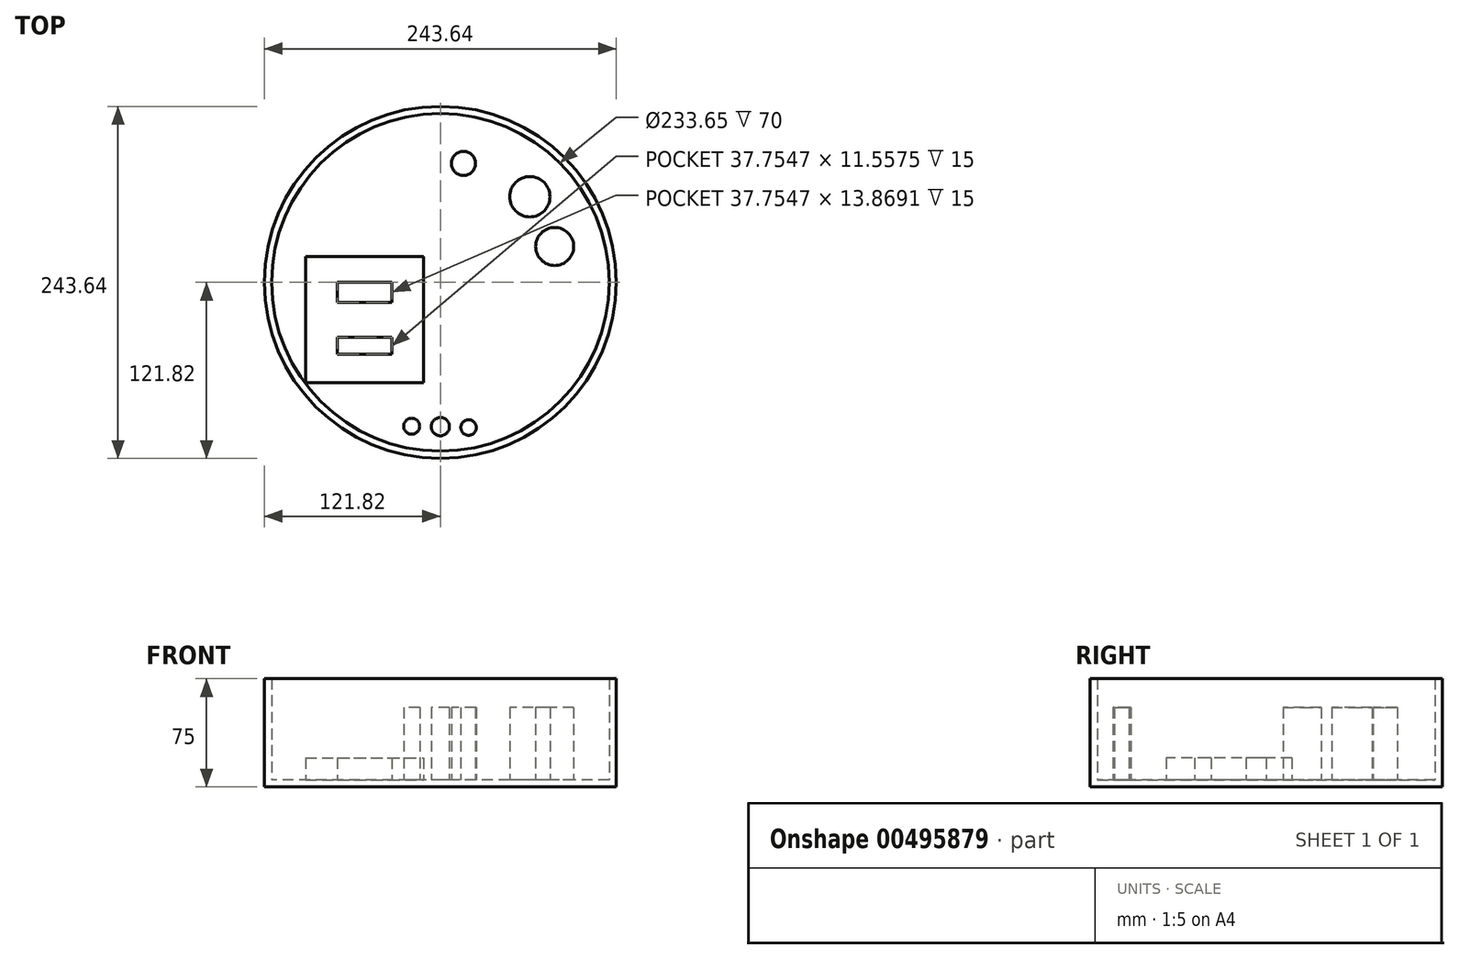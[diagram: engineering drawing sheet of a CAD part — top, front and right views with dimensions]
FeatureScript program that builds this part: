
annotation { "Feature Type Name" : "Feature", "Feature Type Description" : "" }
export const myFeature = defineFeature(function(context is Context, id is Id, definition is map)
    precondition{}
    {
        {
            var Q0;
            Q0=qCreatedBy(makeId("Top.planeOp"),FACE);
            var sketch = newSketch(context, id + "F0", { "sketchPlane" : qUnion([Q0])});
            skCircle(sketch, "E0", {"center": v(0, 0) * mm, "radius": 121.82 * mm});
            skSolve(sketch);
        }
        {
            var Q0;
            Q0=makeQuery(id+"F0.imprint","IMPRINT",FACE,{"disambiguationData":[TD([[makeQuery(id+"F0.imprint","IMPRINT",EDGE,{"derivedFrom":sQuery(id+"F0.wireOp",EDGE,"E0")}),1.0]])]});
            extrude(context, id + "F1", {"entities" : qUnion([Q0]), "depth" : 75 * mm});
        }
        {
            var Q0;
            Q0=makeQuery(id+"F1.opExtrude","CAP_FACE",FACE,{"disambiguationData":[OSD([sQuery(id+"F0.wireOp",EDGE,"E0")])],"isStart":false});
            shell(context, id + "F2", {"entities" : qUnion([Q0]), "thickness" : 5 * mm});
        }
        {
            var Q0;
            {var subQ0=sQuery(id+"F0.wireOp",EDGE,"E0");Q0=makeQuery(id+"F2.opShell","OFFSET_FACE",FACE,{"disambiguationData":[OSD([subQ0]),TDD([makeQuery(id+"F1.opExtrude","CAP_FACE",FACE,{"disambiguationData":[OSD([subQ0])],"isStart":true})])]});}
            var sketch = newSketch(context, id + "F3", { "sketchPlane" : qUnion([Q0])});
            skCircle(sketch, "E1", {"center": v(16.06, 82.36) * mm, "radius": 8.35 * mm});
            skCircle(sketch, "E2", {"center": v(61.91, 59.28) * mm, "radius": 13.96 * mm});
            skCircle(sketch, "E3", {"center": v(79.14, 24.82) * mm, "radius": 13.18 * mm});
            skCircle(sketch, "E4", {"center": v(19.57, -100.46) * mm, "radius": 5.38 * mm});
            skCircle(sketch, "E5", {"center": v(0, -99.88) * mm, "radius": 6.3 * mm});
            skCircle(sketch, "E6", {"center": v(-19.86, -99.59) * mm, "radius": 5.55 * mm});
            skSolve(sketch);
        }
        {
            var Q0;
            Q0=makeQuery(id+"F3.imprint","IMPRINT",FACE,{"disambiguationData":[TD([[makeQuery(id+"F3.imprint","IMPRINT",EDGE,{"derivedFrom":sQuery(id+"F3.wireOp",EDGE,"E1")}),1.0]])]});
            var Q1;
            Q1=makeQuery(id+"F3.imprint","IMPRINT",FACE,{"disambiguationData":[TD([[makeQuery(id+"F3.imprint","IMPRINT",EDGE,{"derivedFrom":sQuery(id+"F3.wireOp",EDGE,"E2")}),1.0]])]});
            var Q2;
            Q2=makeQuery(id+"F3.imprint","IMPRINT",FACE,{"disambiguationData":[TD([[makeQuery(id+"F3.imprint","IMPRINT",EDGE,{"derivedFrom":sQuery(id+"F3.wireOp",EDGE,"E3")}),1.0]])]});
            var Q3;
            Q3=makeQuery(id+"F3.imprint","IMPRINT",FACE,{"disambiguationData":[TD([[makeQuery(id+"F3.imprint","IMPRINT",EDGE,{"derivedFrom":sQuery(id+"F3.wireOp",EDGE,"E4")}),1.0]])]});
            var Q4;
            Q4=makeQuery(id+"F3.imprint","IMPRINT",FACE,{"disambiguationData":[TD([[makeQuery(id+"F3.imprint","IMPRINT",EDGE,{"derivedFrom":sQuery(id+"F3.wireOp",EDGE,"E5")}),1.0]])]});
            var Q5;
            Q5=makeQuery(id+"F3.imprint","IMPRINT",FACE,{"disambiguationData":[TD([[makeQuery(id+"F3.imprint","IMPRINT",EDGE,{"derivedFrom":sQuery(id+"F3.wireOp",EDGE,"E6")}),1.0]])]});
            extrude(context, id + "F4", {"entities" : qUnion([Q0, Q1, Q2, Q3, Q4, Q5]), "operationType" : NewBodyOperationType.ADD, "depth" : 50 * mm});
        }
        {
            var Q0;
            {var subQ0=sQuery(id+"F0.wireOp",EDGE,"E0");Q0=makeQuery(id+"F2.opShell","OFFSET_FACE",FACE,{"disambiguationData":[OSD([subQ0]),TDD([makeQuery(id+"F1.opExtrude","CAP_FACE",FACE,{"disambiguationData":[OSD([subQ0])],"isStart":true})])]});}
            var sketch = newSketch(context, id + "F5", { "sketchPlane" : qUnion([Q0])});
            skLineSegment(sketch, "E7.bottom", {"start": v(-93.23, 17.72) * mm, "end": v(-11.56, 17.72) * mm});
            skLineSegment(sketch, "E7.top", {"start": v(-93.23, -69.35) * mm, "end": v(-11.56, -69.35) * mm});
            skLineSegment(sketch, "E7.left", {"start": v(-93.23, 17.72) * mm, "end": v(-93.23, -69.35) * mm});
            skLineSegment(sketch, "E7.right", {"start": v(-11.56, 17.72) * mm, "end": v(-11.56, -69.35) * mm});
            skPoint(sketch, "E7.middle", {"position": v(-52.4, -25.81) * mm});
            skLineSegment(sketch, "E8.bottom", {"start": v(-71.27, 0) * mm, "end": v(-33.52, 0) * mm});
            skLineSegment(sketch, "E8.top", {"start": v(-71.27, -13.87) * mm, "end": v(-33.52, -13.87) * mm});
            skLineSegment(sketch, "E8.left", {"start": v(-71.27, 0) * mm, "end": v(-71.27, -13.87) * mm});
            skLineSegment(sketch, "E8.right", {"start": v(-33.52, 0) * mm, "end": v(-33.52, -13.87) * mm});
            skPoint(sketch, "E8.middle", {"position": v(-52.4, -6.93) * mm});
            skLineSegment(sketch, "E9.bottom", {"start": v(-71.27, -38.14) * mm, "end": v(-33.52, -38.14) * mm});
            skLineSegment(sketch, "E9.top", {"start": v(-71.27, -49.7) * mm, "end": v(-33.52, -49.7) * mm});
            skLineSegment(sketch, "E9.left", {"start": v(-71.27, -38.14) * mm, "end": v(-71.27, -49.7) * mm});
            skLineSegment(sketch, "E9.right", {"start": v(-33.52, -38.14) * mm, "end": v(-33.52, -49.7) * mm});
            skPoint(sketch, "E9.middle", {"position": v(-52.4, -43.92) * mm});
            skSolve(sketch);
        }
        {
            var Q0;
            Q0=makeQuery(id+"F5.imprint","IMPRINT",FACE,{"disambiguationData":[TD([[makeQuery(id+"F5.imprint","IMPRINT",EDGE,{"derivedFrom":sQuery(id+"F5.wireOp",EDGE,"E7.bottom")}),-1.0]])]});
            extrude(context, id + "F6", {"entities" : qUnion([Q0]), "operationType" : NewBodyOperationType.ADD, "depth" : 15 * mm});
        }
    });
